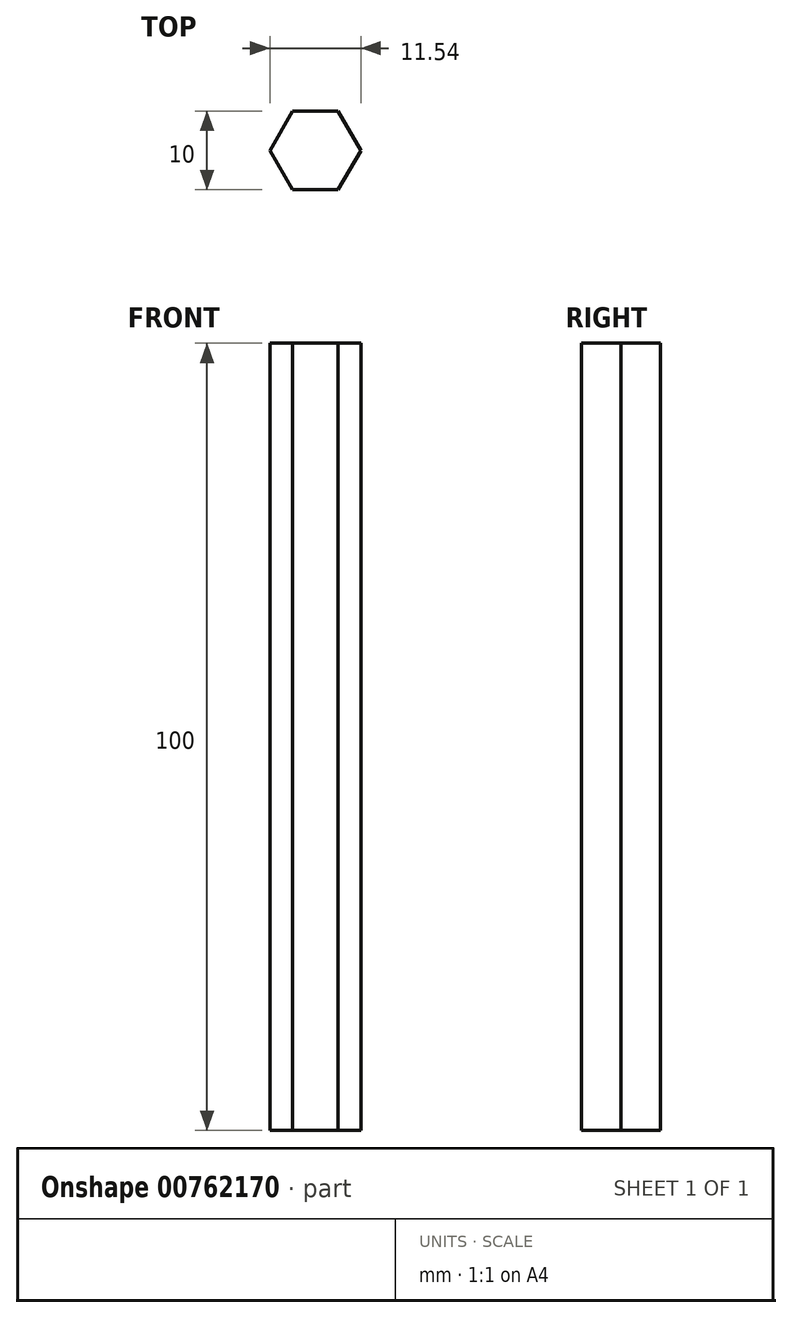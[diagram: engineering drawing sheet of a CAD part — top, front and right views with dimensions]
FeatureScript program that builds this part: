
annotation { "Feature Type Name" : "Feature", "Feature Type Description" : "" }
export const myFeature = defineFeature(function(context is Context, id is Id, definition is map)
    precondition{}
    {
        {
            var Q0;
            Q0=qCreatedBy(makeId("Top.planeOp"),FACE);
            var sketch = newSketch(context, id + "F0", { "sketchPlane" : qUnion([Q0])});
            skCircle(sketch, "E0.cCircle", {"center": v(0, 0) * mm, "radius": 5 * mm, "construction": true});
            skLineSegment(sketch, "E0.0", {"start": v(-2.89, 5) * mm, "end": v(2.89, 5) * mm});
            skLineSegment(sketch, "E0.1", {"start": v(2.89, 5) * mm, "end": v(5.77, 0) * mm});
            skLineSegment(sketch, "E0.2", {"start": v(5.77, 0) * mm, "end": v(2.89, -5) * mm});
            skLineSegment(sketch, "E0.3", {"start": v(2.89, -5) * mm, "end": v(-2.89, -5) * mm});
            skLineSegment(sketch, "E0.4", {"start": v(-2.89, -5) * mm, "end": v(-5.77, 0) * mm});
            skLineSegment(sketch, "E0.5", {"start": v(-5.77, 0) * mm, "end": v(-2.89, 5) * mm});
            skPoint(sketch, "E0.0.midPoint", {"position": v(0, 5) * mm});
            skSolve(sketch);
        }
        {
            var Q0;
            Q0 = qSketchRegion(id + "F0", true);
            extrude(context, id + "F1", {"entities" : qUnion([Q0]), "depth" : 100 * mm, "offsetDistance" : 25.4 * mm});
        }
    });
